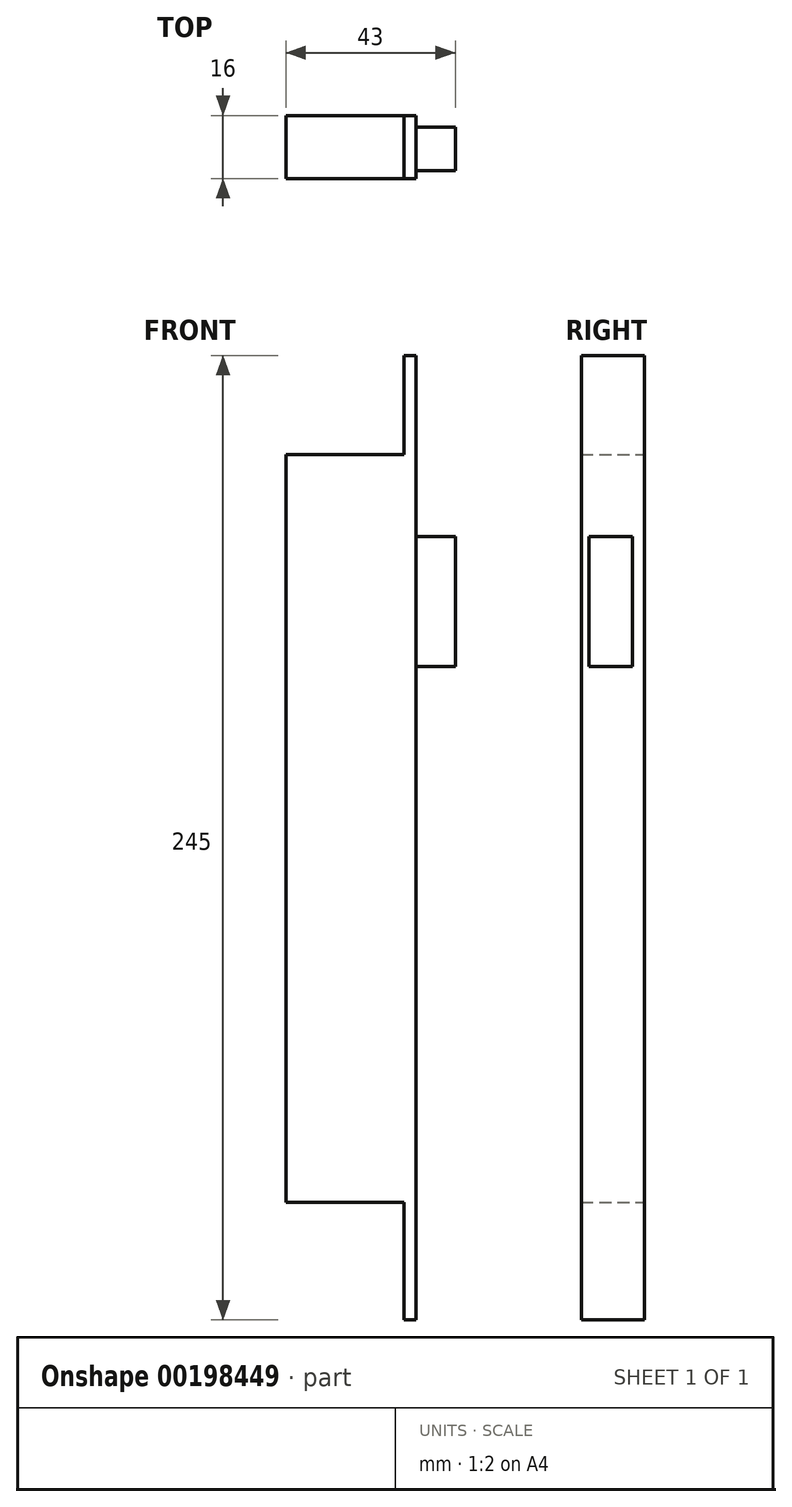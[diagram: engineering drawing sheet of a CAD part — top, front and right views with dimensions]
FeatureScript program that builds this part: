
annotation { "Feature Type Name" : "Feature", "Feature Type Description" : "" }
export const myFeature = defineFeature(function(context is Context, id is Id, definition is map)
    precondition{}
    {
        {
            var Q0;
            Q0=qCreatedBy(makeId("Right.planeOp"),FACE);
            var sketch = newSketch(context, id + "F0", { "sketchPlane" : qUnion([Q0])});
            skLineSegment(sketch, "E0.bottom", {"start": v(0, 0) * mm, "end": v(16, 0) * mm});
            skLineSegment(sketch, "E0.top", {"start": v(0, -190) * mm, "end": v(16, -190) * mm});
            skLineSegment(sketch, "E0.left", {"start": v(0, 0) * mm, "end": v(0, -190) * mm});
            skLineSegment(sketch, "E0.right", {"start": v(16, 0) * mm, "end": v(16, -190) * mm});
            skSolve(sketch);
        }
        {
            var Q0;
            Q0=makeQuery(id+"F0.imprint","IMPRINT",FACE,{"disambiguationData":[TD([[makeQuery(id+"F0.imprint","IMPRINT",EDGE,{"derivedFrom":sQuery(id+"F0.wireOp",EDGE,"E0.bottom")}),-1.0]])]});
            extrude(context, id + "F1", {"entities" : qUnion([Q0]), "depth" : 30 * mm});
        }
        {
            var Q0;
            Q0=makeQuery(id+"F1.opExtrude","CAP_FACE",FACE,{"disambiguationData":[OSD([sQuery(id+"F0.wireOp",EDGE,"E0.bottom"),sQuery(id+"F0.wireOp",EDGE,"E0.top"),sQuery(id+"F0.wireOp",EDGE,"E0.left"),sQuery(id+"F0.wireOp",EDGE,"E0.right")])],"isStart":false});
            var sketch = newSketch(context, id + "F2", { "sketchPlane" : qUnion([Q0])});
            skSolve(sketch);
        }
        {
            var Q0;
            Q0=makeQuery(id+"F2.imprint","IMPRINT",FACE,{"disambiguationData":[TD([[makeQuery(id+"F2.imprint","IMPRINT",EDGE,{"derivedFrom":makeQuery(id+"F1.opExtrude","CAP_EDGE",EDGE,{"disambiguationData":[OSD([sQuery(id+"F0.wireOp",EDGE,"E0.bottom")])],"isStart":false})}),-1.0]])]});
            var sketch = newSketch(context, id + "F3", { "sketchPlane" : qUnion([Q0])});
            skLineSegment(sketch, "E1.bottom", {"start": v(0, 25.16) * mm, "end": v(16, 25.16) * mm});
            skLineSegment(sketch, "E1.top", {"start": v(0, -219.84) * mm, "end": v(16, -219.84) * mm});
            skLineSegment(sketch, "E1.left", {"start": v(0, 25.16) * mm, "end": v(0, -219.84) * mm});
            skLineSegment(sketch, "E1.right", {"start": v(16, 25.16) * mm, "end": v(16, -219.84) * mm});
            skSolve(sketch);
        }
        {
            var Q0;
            Q0 = qSketchRegion(id + "F2", true);
            var Q1;
            Q1 = qSketchRegion(id + "F3", true);
            extrude(context, id + "F4", {"entities" : qUnion([Q0, Q1]), "operationType" : NewBodyOperationType.ADD, "depth" : 3 * mm});
        }
        {
            var Q0;
            Q0=makeQuery(id+"F4.opExtrude","CAP_FACE",FACE,{"disambiguationData":[OSD([sQuery(id+"F3.wireOp",EDGE,"E1.bottom"),sQuery(id+"F3.wireOp",EDGE,"E1.top"),sQuery(id+"F3.wireOp",EDGE,"E1.left"),sQuery(id+"F3.wireOp",EDGE,"E1.right")])],"isStart":false});
            var sketch = newSketch(context, id + "F5", { "sketchPlane" : qUnion([Q0])});
            skLineSegment(sketch, "E2.bottom", {"start": v(2, -20.84) * mm, "end": v(13, -20.84) * mm});
            skLineSegment(sketch, "E2.top", {"start": v(2, -53.84) * mm, "end": v(13, -53.84) * mm});
            skLineSegment(sketch, "E2.left", {"start": v(2, -20.84) * mm, "end": v(2, -53.84) * mm});
            skLineSegment(sketch, "E2.right", {"start": v(13, -20.84) * mm, "end": v(13, -53.84) * mm});
            skSolve(sketch);
        }
        {
            var Q0;
            Q0=makeQuery(id+"F5.imprint","IMPRINT",FACE,{"disambiguationData":[TD([[makeQuery(id+"F5.imprint","IMPRINT",EDGE,{"derivedFrom":sQuery(id+"F5.wireOp",EDGE,"E2.bottom")}),-1.0]])]});
            extrude(context, id + "F6", {"entities" : qUnion([Q0]), "operationType" : NewBodyOperationType.ADD, "depth" : 10 * mm});
        }
    });
